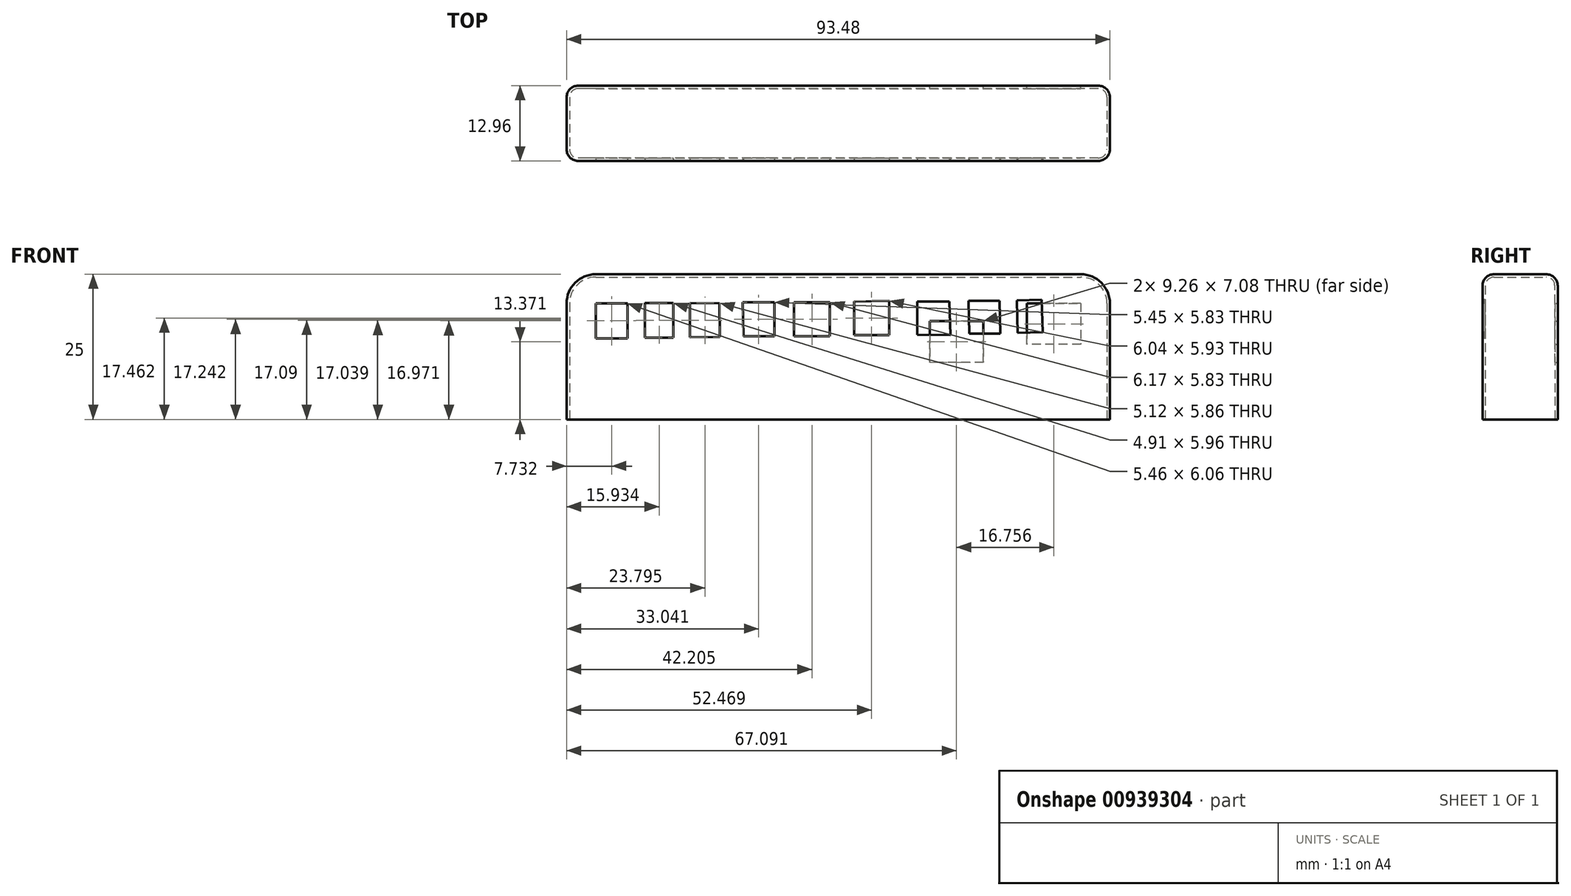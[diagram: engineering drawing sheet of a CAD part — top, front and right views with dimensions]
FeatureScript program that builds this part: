
annotation { "Feature Type Name" : "Feature", "Feature Type Description" : "" }
export const myFeature = defineFeature(function(context is Context, id is Id, definition is map)
    precondition{}
    {
        {
            var Q0;
            Q0=qCreatedBy(makeId("Top.planeOp"),FACE);
            var sketch = newSketch(context, id + "F0", { "sketchPlane" : qUnion([Q0])});
            skLineSegment(sketch, "E0.bottom", {"start": v(46.74, 6.48) * mm, "end": v(-46.74, 6.48) * mm});
            skLineSegment(sketch, "E0.top", {"start": v(46.74, -6.48) * mm, "end": v(-46.74, -6.48) * mm});
            skLineSegment(sketch, "E0.left", {"start": v(46.74, 6.48) * mm, "end": v(46.74, -6.48) * mm});
            skLineSegment(sketch, "E0.right", {"start": v(-46.74, 6.48) * mm, "end": v(-46.74, -6.48) * mm});
            skPoint(sketch, "E0.middle", {"position": v(0, 0) * mm});
            skSolve(sketch);
        }
        {
            var Q0;
            Q0 = qSketchRegion(id + "F0", true);
            extrude(context, id + "F1", {"entities" : qUnion([Q0]), "depth" : 25 * mm, "offsetDistance" : 25.4 * mm});
        }
        {
            var Q0;
            Q0=makeQuery(id+"F1.opExtrude","CAP_EDGE",EDGE,{"disambiguationData":[OSD([sQuery(id+"F0.wireOp",EDGE,"E0.left")])],"isStart":false});
            fillet(context, id + "F2", {"entities" : qUnion([Q0]), "radius" : 5 * mm, "tangentPropagation" : true, "allowEdgeOverflow" : false});
        }
        {
            var Q0;
            Q0=makeQuery(id+"F1.opExtrude","CAP_EDGE",EDGE,{"disambiguationData":[OSD([sQuery(id+"F0.wireOp",EDGE,"E0.right")])],"isStart":false});
            fillet(context, id + "F3", {"entities" : qUnion([Q0]), "radius" : 5 * mm, "tangentPropagation" : true, "allowEdgeOverflow" : false});
        }
        {
            var Q0;
            Q0=makeQuery(id+"F1.opExtrude","CAP_EDGE",EDGE,{"disambiguationData":[OSD([sQuery(id+"F0.wireOp",EDGE,"E0.top")])],"isStart":false});
            var Q1;
            Q1=makeQuery(id+"F1.opExtrude","CAP_EDGE",EDGE,{"disambiguationData":[OSD([sQuery(id+"F0.wireOp",EDGE,"E0.bottom")])],"isStart":false});
            var Q2;
            Q2=makeQuery(id+"F1.opExtrude","SWEPT_EDGE",EDGE,{"disambiguationData":[OSD([sQuery(id+"F0.wireOp",EDGE,"E0.bottom"),sQuery(id+"F0.wireOp",EDGE,"E0.left")])]});
            var Q3;
            Q3=makeQuery(id+"F1.opExtrude","SWEPT_EDGE",EDGE,{"disambiguationData":[OSD([sQuery(id+"F0.wireOp",EDGE,"E0.top"),sQuery(id+"F0.wireOp",EDGE,"E0.left")])]});
            var Q4;
            Q4=makeQuery(id+"F1.opExtrude","SWEPT_EDGE",EDGE,{"disambiguationData":[OSD([sQuery(id+"F0.wireOp",EDGE,"E0.top"),sQuery(id+"F0.wireOp",EDGE,"E0.right")])]});
            var Q5;
            {var subQ0=sQuery(id+"F0.wireOp",EDGE,"E0.right");var subQ1=sQuery(id+"F0.wireOp",EDGE,"E0.bottom");Q5=makeQuery(id+"F8ZiKZxwUii9QuQ_1.opShell","OFFSET_EDGE",EDGE,{"disambiguationData":[OSD([subQ1,subQ0]),TDD([makeQuery(id+"F1.opExtrude","SWEPT_EDGE",EDGE,{"disambiguationData":[OSD([subQ1,subQ0])]})])]});}
            fillet(context, id + "F4", {"entities" : qUnion([Q0, Q1, Q2, Q3, Q4, Q5]), "radius" : 2 * mm, "tangentPropagation" : true, "allowEdgeOverflow" : false});
        }
        {
            var Q0;
            Q0=makeQuery(id+"F1.opExtrude","CAP_FACE",FACE,{"disambiguationData":[OSD([sQuery(id+"F0.wireOp",EDGE,"E0.bottom"),sQuery(id+"F0.wireOp",EDGE,"E0.top"),sQuery(id+"F0.wireOp",EDGE,"E0.left"),sQuery(id+"F0.wireOp",EDGE,"E0.right")])],"isStart":true});
            shell(context, id + "F5", {"entities" : qUnion([Q0]), "thickness" : 0.5 * mm});
        }
        {
            var Q0;
            Q0=makeQuery(id+"F1.opExtrude","SWEPT_FACE",FACE,{"disambiguationData":[OSD([sQuery(id+"F0.wireOp",EDGE,"E0.top")])]});
            var sketch = newSketch(context, id + "F6", { "sketchPlane" : qUnion([Q0])});
            skLineSegment(sketch, "E1", {"start": v(-41.74, 20) * mm, "end": v(-36.28, 20) * mm});
            skLineSegment(sketch, "E2", {"start": v(-36.28, 13.94) * mm, "end": v(-41.74, 13.94) * mm});
            skLineSegment(sketch, "E3", {"start": v(-41.74, 13.94) * mm, "end": v(-41.74, 20) * mm});
            skLineSegment(sketch, "E4", {"start": v(-36.28, 20) * mm, "end": v(-36.28, 13.94) * mm});
            skLineSegment(sketch, "E5", {"start": v(-33.26, 20.02) * mm, "end": v(-33.26, 14.06) * mm});
            skLineSegment(sketch, "E6", {"start": v(-33.26, 14.06) * mm, "end": v(-28.35, 14.06) * mm});
            skLineSegment(sketch, "E7", {"start": v(-28.35, 14.06) * mm, "end": v(-28.35, 20.02) * mm});
            skLineSegment(sketch, "E8", {"start": v(-33.26, 20.02) * mm, "end": v(-28.35, 20.02) * mm});
            skLineSegment(sketch, "E9", {"start": v(-25.5, 14.16) * mm, "end": v(-20.39, 14.2) * mm});
            skLineSegment(sketch, "E10", {"start": v(-25.5, 14.16) * mm, "end": v(-25.5, 20.02) * mm});
            skLineSegment(sketch, "E11", {"start": v(-20.39, 14.2) * mm, "end": v(-20.44, 20) * mm});
            skLineSegment(sketch, "E12", {"start": v(-20.44, 20) * mm, "end": v(-25.5, 20.02) * mm});
            skLineSegment(sketch, "E13", {"start": v(-16.32, 14.33) * mm, "end": v(-10.97, 14.33) * mm});
            skLineSegment(sketch, "E14", {"start": v(-10.97, 14.33) * mm, "end": v(-10.97, 20.16) * mm});
            skLineSegment(sketch, "E15", {"start": v(-10.97, 20.16) * mm, "end": v(-16.43, 20.16) * mm});
            skLineSegment(sketch, "E16", {"start": v(-16.43, 20.16) * mm, "end": v(-16.32, 14.33) * mm});
            skLineSegment(sketch, "E17", {"start": v(-7.62, 14.33) * mm, "end": v(-1.45, 14.33) * mm});
            skLineSegment(sketch, "E18", {"start": v(-1.45, 14.33) * mm, "end": v(-1.45, 20.16) * mm});
            skLineSegment(sketch, "E19", {"start": v(-1.45, 20.16) * mm, "end": v(-7.62, 20.16) * mm});
            skLineSegment(sketch, "E20", {"start": v(-7.62, 14.33) * mm, "end": v(-7.62, 20.16) * mm});
            skLineSegment(sketch, "E21", {"start": v(2.71, 14.5) * mm, "end": v(8.75, 14.5) * mm});
            skLineSegment(sketch, "E22", {"start": v(8.75, 14.5) * mm, "end": v(8.75, 20.43) * mm});
            skLineSegment(sketch, "E23", {"start": v(2.71, 20.29) * mm, "end": v(8.75, 20.43) * mm});
            skLineSegment(sketch, "E24", {"start": v(2.71, 14.5) * mm, "end": v(2.71, 20.29) * mm});
            skLineSegment(sketch, "E25", {"start": v(13.6, 20.29) * mm, "end": v(19.13, 20.29) * mm});
            skLineSegment(sketch, "E26", {"start": v(13.6, 20.29) * mm, "end": v(13.6, 14.57) * mm});
            skLineSegment(sketch, "E27", {"start": v(19.3, 14.54) * mm, "end": v(19.13, 20.29) * mm});
            skLineSegment(sketch, "E28", {"start": v(13.6, 14.57) * mm, "end": v(19.3, 14.54) * mm});
            skLineSegment(sketch, "E29", {"start": v(22.53, 14.78) * mm, "end": v(22.4, 20.44) * mm});
            skLineSegment(sketch, "E30", {"start": v(22.53, 14.78) * mm, "end": v(27.88, 14.78) * mm});
            skLineSegment(sketch, "E31", {"start": v(27.88, 14.78) * mm, "end": v(27.75, 20.44) * mm});
            skLineSegment(sketch, "E32", {"start": v(22.4, 20.44) * mm, "end": v(27.75, 20.44) * mm});
            skLineSegment(sketch, "E33", {"start": v(30.88, 14.9) * mm, "end": v(35.2, 15.04) * mm});
            skLineSegment(sketch, "E34", {"start": v(35.2, 15.04) * mm, "end": v(35.02, 20.63) * mm});
            skLineSegment(sketch, "E35", {"start": v(30.88, 14.9) * mm, "end": v(30.71, 20.6) * mm});
            skLineSegment(sketch, "E36", {"start": v(35.02, 20.63) * mm, "end": v(30.71, 20.5) * mm});
            skSolve(sketch);
        }
        {
            var Q0;
            Q0 = qSketchRegion(id + "F6", true);
            extrude(context, id + "F7", {"entities" : qUnion([Q0]), "operationType" : NewBodyOperationType.REMOVE, "oppositeDirection" : true, "depth" : 10 * mm, "offsetDistance" : 25 * mm});
        }
        {
            var Q0;
            Q0=makeQuery(id+"F1.opExtrude","SWEPT_FACE",FACE,{"disambiguationData":[OSD([sQuery(id+"F0.wireOp",EDGE,"E0.bottom")])]});
            var sketch = newSketch(context, id + "F8", { "sketchPlane" : qUnion([Q0])});
            skLineSegment(sketch, "E37.bottom", {"start": v(-41.74, 20) * mm, "end": v(-32.48, 20) * mm});
            skLineSegment(sketch, "E37.top", {"start": v(-41.74, 12.92) * mm, "end": v(-32.48, 12.92) * mm});
            skLineSegment(sketch, "E37.left", {"start": v(-41.74, 20) * mm, "end": v(-41.74, 12.92) * mm});
            skLineSegment(sketch, "E37.right", {"start": v(-32.48, 20) * mm, "end": v(-32.48, 12.92) * mm});
            skLineSegment(sketch, "E38.bottom", {"start": v(-24.98, 16.91) * mm, "end": v(-15.72, 16.91) * mm});
            skLineSegment(sketch, "E38.top", {"start": v(-24.98, 9.83) * mm, "end": v(-15.72, 9.83) * mm});
            skLineSegment(sketch, "E38.left", {"start": v(-24.98, 16.91) * mm, "end": v(-24.98, 9.83) * mm});
            skLineSegment(sketch, "E38.right", {"start": v(-15.72, 16.91) * mm, "end": v(-15.72, 9.83) * mm});
            skSolve(sketch);
        }
        {
            var Q0;
            Q0 = qSketchRegion(id + "F8", true);
            extrude(context, id + "F9", {"entities" : qUnion([Q0]), "operationType" : NewBodyOperationType.REMOVE, "oppositeDirection" : true, "depth" : 5 * mm, "offsetDistance" : 25 * mm});
        }
    });
